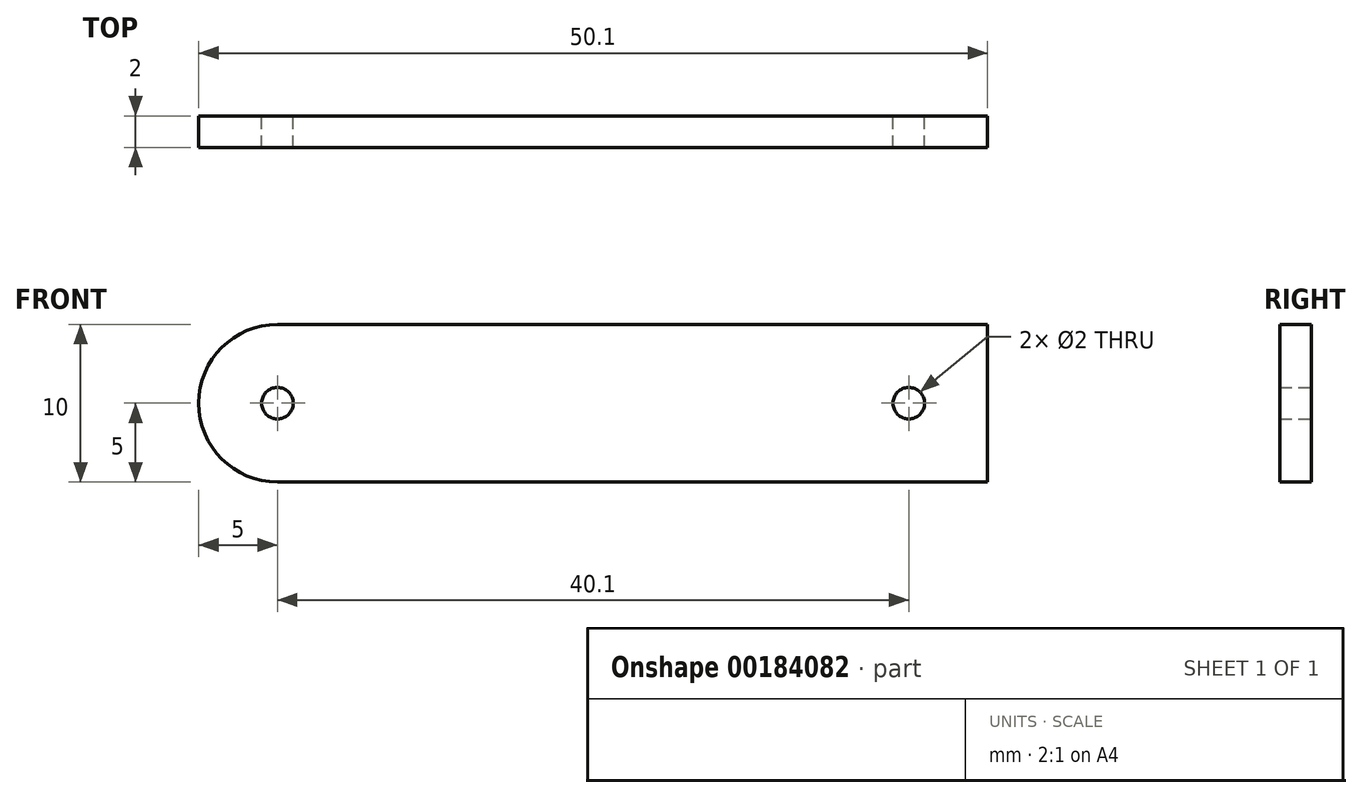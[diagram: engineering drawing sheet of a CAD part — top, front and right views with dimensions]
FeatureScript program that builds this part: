
annotation { "Feature Type Name" : "Feature", "Feature Type Description" : "" }
export const myFeature = defineFeature(function(context is Context, id is Id, definition is map)
    precondition{}
    {
        {
            var Q0;
            Q0=qCreatedBy(makeId("Front.planeOp"),FACE);
            var sketch = newSketch(context, id + "F0", { "sketchPlane" : qUnion([Q0])});
            skLineSegment(sketch, "E0.bottom", {"start": v(0, 0) * mm, "end": v(45.1, 0) * mm});
            skLineSegment(sketch, "E0.top", {"start": v(0, -10) * mm, "end": v(45.1, -10) * mm});
            skLineSegment(sketch, "E0.right", {"start": v(45.1, 0) * mm, "end": v(45.1, -10) * mm});
            skArc(sketch, "E1", {"start": v(0, 0) * mm, "mid": v(-5, -5) * mm, "end": v(0, -10) * mm});
            skCircle(sketch, "E2", {"center": v(0, -5) * mm, "radius": 1 * mm});
            skCircle(sketch, "E3", {"center": v(40.1, -5) * mm, "radius": 1 * mm});
            skSolve(sketch);
        }
        {
            var Q0;
            Q0=makeQuery(id+"F0.imprint","IMPRINT",FACE,{"disambiguationData":[TD([[makeQuery(id+"F0.imprint","IMPRINT",EDGE,{"derivedFrom":sQuery(id+"F0.wireOp",EDGE,"E0.bottom")}),-1.0]])]});
            extrude(context, id + "F1", {"entities" : qUnion([Q0]), "depth" : 2 * mm});
        }
    });
